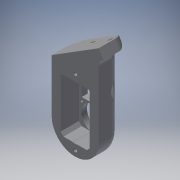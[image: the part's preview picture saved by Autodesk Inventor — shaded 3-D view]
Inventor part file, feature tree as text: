
AUTODESK INVENTOR PART (.ipt)
format: ipt  version: 2018 (Build 220112000, 112)  size: 832,512 bytes
history: native  units: mm
features: sketch x33, extrude x26, projected_geometry x23, fillet x9, hole x7, chamfer x5, other x3, mirror x1, plane x1, reference x1
ambient origin geometry x8: Origin, YZ Plane, XZ Plane, XY Plane, X Axis, Y Axis, Z Axis, Center Point
bodies: Solid1 (feature_tree)
feature tree (109):
  extrude  "Extrusion1"  Depth=45.0mm
  extrude  "Extrusion2"  Depth=1.95mm
  hole  "Hole1"  [1 undecoded]
  hole  "Hole2"  [1 undecoded]
  fillet  "Fillet1"  Radius=14.0mm
  extrude  "Extrusion3"  Depth=18.5mm
  extrude  "Extrusion4"  Depth=20.5mm
  extrude  "Extrusion5"  Depth=2.195mm
  extrude  "Extrusion6"  Depth=20.5mm
  hole  "Hole3"  [1 undecoded]
  extrude  "Extrusion7"  Depth=0.5mm
  extrude  "Extrusion8"  Depth=5.0mm TaperAngle=0.0deg
  extrude  "Extrusion9"  Depth=24.5mm
  extrude  "Extrusion10"  Depth=10.0mm
  extrude  "Extrusion11"  Depth=14.5mm
  extrude  "Extrusion12"  Depth=14.5mm
  extrude  "Extrusion13"  Depth=5.0mm
  extrude  "Extrusion14"  Depth=2.25mm
  extrude  "Extrusion15"  Depth=5.0mm
  extrude  "Extrusion16"  Depth=9.0mm
  extrude  "Extrusion17"  Depth=4.0mm
  chamfer  "Chamfer1"  Distance=1.0mm
  fillet  "Fillet7"  Radius=20.7mm
  fillet  "Fillet8"  Radius=32.0mm
  mirror  "Mirror1"
  extrude  "Extrusion18"  Depth=1.0mm TaperAngle=0.0deg
  extrude  "Extrusion19"  Depth=8.0mm
  extrude  "Extrusion20"  Depth=0.2mm TaperAngle=0.0deg
  extrude  "Extrusion21"  Depth=0.5mm TaperAngle=0.0deg
  extrude  "Extrusion22"  Depth=5.0mm TaperAngle=0.0deg
  extrude  "Extrusion23"  Depth=0.2mm TaperAngle=0.0deg
  chamfer  "Chamfer3"  Distance=0.2mm
  chamfer  "Chamfer4"  Distance=2.5mm Angle=45.0deg
  fillet  "Fillet12"  Radius=1.5mm
  fillet  "Fillet15"  Radius=0.5mm
  hole  "Hole6"  [1 undecoded]
  extrude  "Extrusion24"  Depth=25.0mm
  fillet  "Fillet16"  Radius=25.0mm
  chamfer  "Chamfer5"  Distance=25.0mm
  hole  "Hole7"  [1 undecoded]
  extrude  "Extrusion25"  Depth=2.0mm TaperAngle=0.0deg
  fillet  "Fillet18"  Radius=7.0mm
  fillet  "Fillet19"  Radius=4.0mm
  hole  "Hole8"  [1 undecoded]
  plane  "Work Plane1"
  hole  "Hole9"  [1 undecoded]
  fillet  "Fillet20"  Radius=4.9mm
  extrude  "Extrusion26"  Depth=4.9mm
  chamfer  "Chamfer6"  Distance=5.7mm
  sketch  "Sketch1"  dims[d0=24.5mm d1=45.0mm]
  sketch  "Sketch2"  dims[d2=1.95mm d3=0.0mm d4=2.25mm]
  projected_geometry  "Projected Loop1"
  sketch  "Sketch3"  dims[d5=20.0mm d6=2.25mm]
  projected_geometry  "Projected Loop2"
  sketch  "Sketch4"  dims[d7=5.25mm d8=5.25mm d9=14.0mm]
  projected_geometry  "Projected Loop3"
  sketch  "Sketch5"  dims[d10=5.25mm d11=18.5mm]
  projected_geometry  "Projected Loop4"
  sketch  "Sketch6"  dims[d12=10.0mm d13=0.0mm d14=20.5mm]
  projected_geometry  "Projected Loop5"
  sketch  "Sketch7"  dims[d15=2.0mm d16=2.195mm]
  projected_geometry  "Projected Loop6"
  sketch  "Sketch8"  dims[d17=2.0mm]
  projected_geometry  "Projected Loop7"
  sketch  "Sketch9"  dims[d18=2.4mm d19=6.0mm d20=4.4mm d21=2.0mm d22=90.0deg d23=8.0mm d24=20.594885mm d25=20.5mm]
  projected_geometry  "Projected Loop8"
  projected_geometry  "Projected Loop9"
  sketch  "Sketch10"  dims[d26=26.65mm d27=2.0mm]
  projected_geometry  "Projected Loop10"
  projected_geometry  "Projected Loop11"
  sketch  "Sketch11"  dims[d28=2.0mm]
  projected_geometry  "Projected Loop12"
  sketch  "Sketch12"  dims[d29=2.4mm d30=6.0mm d31=4.4mm d32=2.0mm d33=90.0deg d34=8.0mm d35=20.594885mm d36=0.5mm]
  sketch  "Sketch13"  dims[d37=18.0mm d38=5.0mm d39=0.0mm]
  sketch  "Sketch14"  dims[d41=10.0mm d42=0.0mm d43=24.5mm]
  projected_geometry  "Projected Loop13"
  sketch  "Sketch15"  dims[d44=1.15mm d45=0.0mm d46=10.0mm]
  sketch  "Sketch16"  dims[d47=21.0mm d48=14.5mm]
  projected_geometry  "Projected Loop14"
  sketch  "Sketch17"  dims[d49=20.0mm d50=14.5mm]
  projected_geometry  "Projected Loop15"
  sketch  "Sketch18"  dims[d51=24.5mm d52=5.0mm]
  projected_geometry  "Projected Loop16"
  sketch  "Sketch19"  dims[d53=5.0mm d54=2.25mm]
  projected_geometry  "Projected Loop17"
  sketch  "Sketch20"  dims[d55=2.25mm d56=5.0mm]
  projected_geometry  "Projected Loop18"
  sketch  "Sketch22"  dims[d57=5.0mm d58=9.0mm]
  sketch  "Sketch26"  dims[d59=14.75mm d60=4.0mm d61=1.0mm d62=0.0mm d63=20.7mm]
  sketch  "Sketch27"  dims[d64=2.4mm d65=6.0mm d66=4.4mm d67=2.0mm d68=90.0deg d69=8.0mm d70=20.594885mm d72=32.0mm]
  projected_geometry  "Projected Loop22"
  sketch  "Sketch28"  dims[d73=5.0mm d74=0.0mm d75=1.0mm d76=0.0mm]
  sketch  "Sketch29"  dims[d77=12.25mm d78=0.0mm d80=8.0mm]
  sketch  "Sketch31"  dims[d81=4.5mm d82=0.0mm d84=0.2mm d85=0.0mm]
  projected_geometry  "Projected Loop24"
  sketch  "Sketch32"  dims[d86=21.0mm d87=0.5mm d88=0.0mm]
  reference  "Reference1"
  sketch  "Sketch33"  dims[d91=8.0mm d92=0.0mm d93=5.0mm d94=0.0mm]
  sketch  "Sketch34"  dims[d95=5.0mm d96=0.0mm d98=0.2mm d99=0.0mm d100=0.2mm d101=0.0mm d102=2.5mm d103=2.0mm d104=45.0deg d105=1.5mm d114=0.5mm]
  projected_geometry  "Projected Loop25"
  sketch  "Sketch35"  dims[d115=22.55mm d116=0.0mm d128=40.0mm]
  sketch  "Sketch36"  dims[d129=70.0mm d130=25.0mm d131=25.0mm d132=0.0mm d133=25.0mm d134=0.0mm]
  projected_geometry  "Projected Loop26"
  sketch  "Sketch37"  dims[d135=25.0mm d136=0.0mm d137=2.0mm d138=0.0mm]
  sketch  "Sketch38"  dims[d143=8.0mm d144=2.0mm d145=0.0mm d148=7.0mm d149=2.0mm d150=45.0deg d152=4.0mm d153=2.0mm d154=45.0deg d155=8.0mm d158=8.0mm d159=4.9mm d160=4.9mm d161=3.2mm d162=6.0mm d163=6.3mm d164=2.0mm d165=90.0deg d166=8.0mm d167=20.594885mm d168=5.7mm d169=11.0mm d170=0.0mm d171=0.7mm d173=2.0mm d174=2.0mm d175=45.0deg d176=6.0mm d177=3.2mm d178=7.01mm d179=6.3mm d180=2.0mm d181=90.0deg d182=10.979mm d183=20.594885mm d184=5.7mm d185=11.0mm d186=0.0mm d187=1.5mm d188=1.5mm d189=14.0mm d190=17.0mm d191=5.0mm d192=3.3mm d193=6.0mm d194=3.023mm d195=2.0mm d196=14.3117mm d197=8.0mm d198=20.594885mm d199=-100.0mm d200=5.7mm d201=6.0mm d202=3.023mm d203=2.0mm d204=14.3117mm d205=96.0mm d206=0.0mm d207=1.0mm d208=16.0mm d209=2.0mm d210=0.0mm d211=1.5mm d212=2.0mm d213=45.0deg]
  projected_geometry  "Projected Loop27"
  parser-record x1  (decoder bookkeeping rows leaked as tree rows — omitted from the tree; the rows remain in map.json)
  other  "bottomarm.iam"
  other  "arm1:1"
note: 7 required parameter values undecoded (feature->parameter linkage not recoverable at this tier; creation-order binding heuristic only, values carry confidence <= 0.55)
note: 1 file-system path scrubbed to <path> (originals preserved in map.json)
